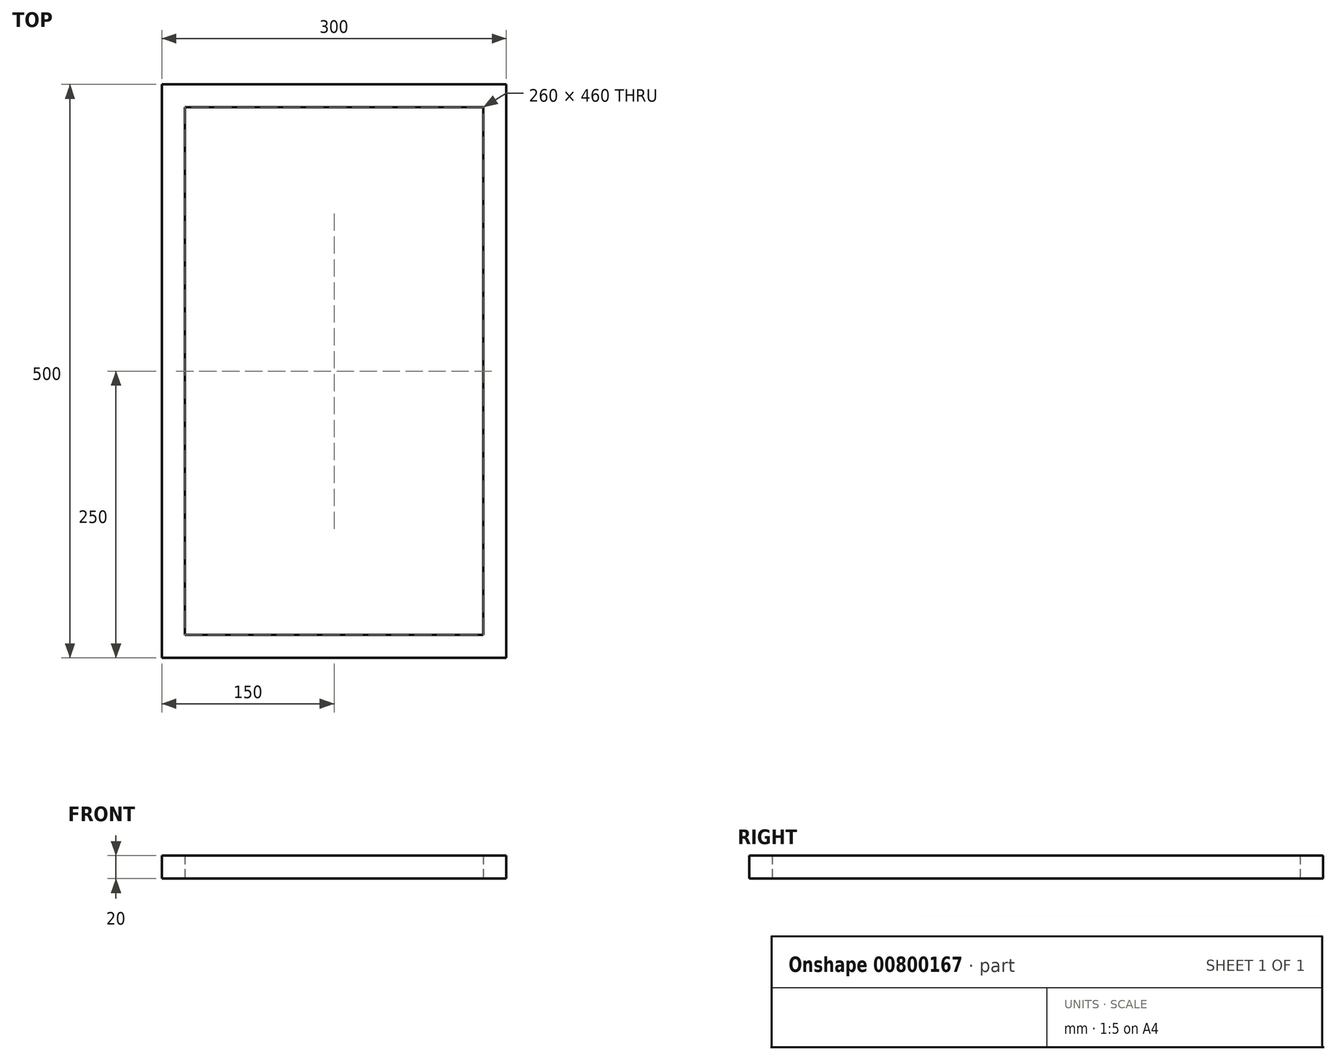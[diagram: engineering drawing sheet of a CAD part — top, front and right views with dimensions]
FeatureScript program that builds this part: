
annotation { "Feature Type Name" : "Feature", "Feature Type Description" : "" }
export const myFeature = defineFeature(function(context is Context, id is Id, definition is map)
    precondition{}
    {
        {
            var Q0;
            Q0=qCreatedBy(makeId("Top.planeOp"),FACE);
            var sketch = newSketch(context, id + "F0", { "sketchPlane" : qUnion([Q0])});
            skLineSegment(sketch, "E0.bottom", {"start": v(150, 0) * mm, "end": v(-150, 0) * mm});
            skLineSegment(sketch, "E0.top", {"start": v(150, 500) * mm, "end": v(-150, 500) * mm});
            skLineSegment(sketch, "E0.left", {"start": v(150, 0) * mm, "end": v(150, 500) * mm});
            skLineSegment(sketch, "E0.right", {"start": v(-150, 0) * mm, "end": v(-150, 500) * mm});
            skPoint(sketch, "E0.middle", {"position": v(0, 250) * mm});
            skLineSegment(sketch, "E1.bottom", {"start": v(130, 20) * mm, "end": v(-130, 20) * mm});
            skLineSegment(sketch, "E1.top", {"start": v(130, 480) * mm, "end": v(-130, 480) * mm});
            skLineSegment(sketch, "E1.left", {"start": v(130, 20) * mm, "end": v(130, 480) * mm});
            skLineSegment(sketch, "E1.right", {"start": v(-130, 20) * mm, "end": v(-130, 480) * mm});
            skSolve(sketch);
        }
        {
            var Q0;
            Q0=makeQuery(id+"F0.imprint","IMPRINT",FACE,{"disambiguationData":[TD([[makeQuery(id+"F0.imprint","IMPRINT",EDGE,{"derivedFrom":sQuery(id+"F0.wireOp",EDGE,"E0.bottom")}),-1.0]])]});
            extrude(context, id + "F1", {"entities" : qUnion([Q0]), "depth" : 20 * mm, "offsetDistance" : 25 * mm});
        }
    });
